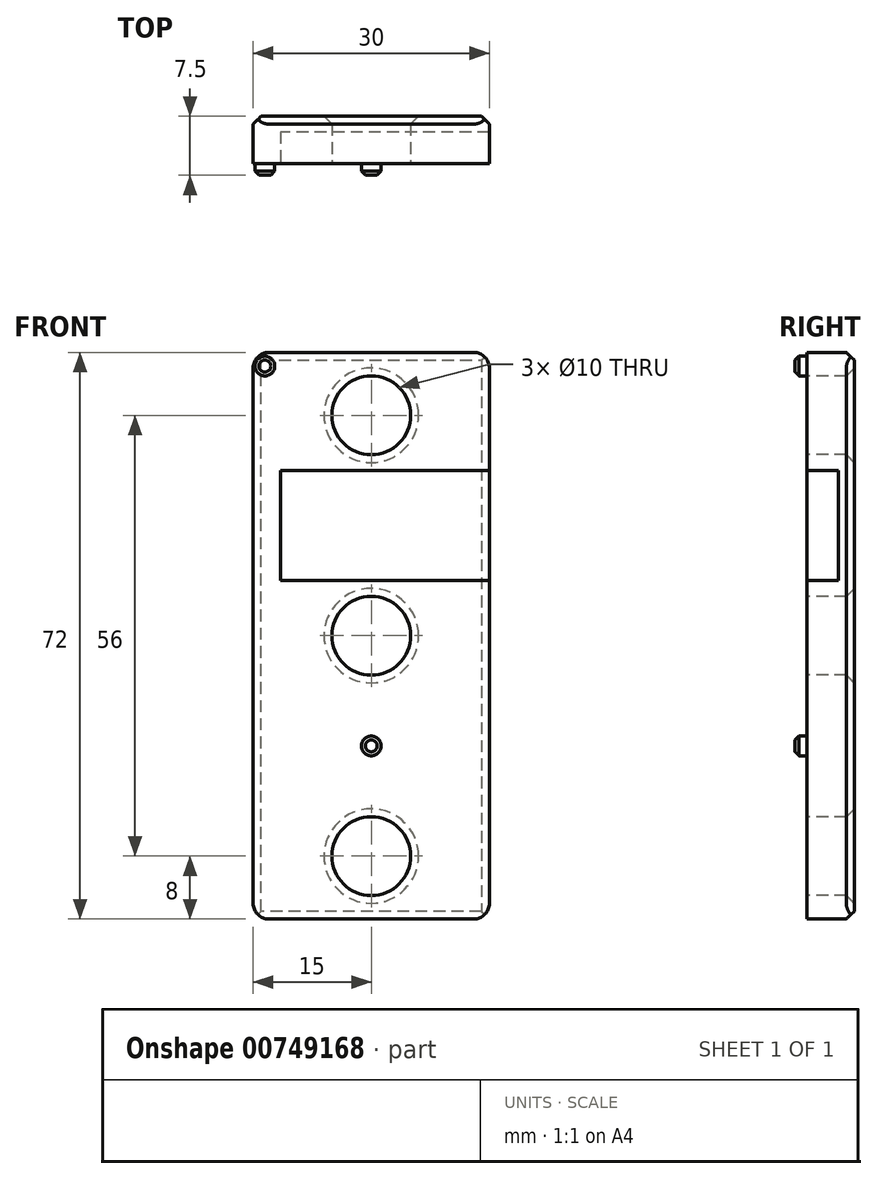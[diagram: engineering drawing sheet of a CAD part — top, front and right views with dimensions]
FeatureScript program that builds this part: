
annotation { "Feature Type Name" : "Feature", "Feature Type Description" : "" }
export const myFeature = defineFeature(function(context is Context, id is Id, definition is map)
    precondition{}
    {
        {
            var Q0;
            Q0=qCreatedBy(makeId("Front.planeOp"),FACE);
            var sketch = newSketch(context, id + "F0", { "sketchPlane" : qUnion([Q0])});
            skLineSegment(sketch, "E0.bottom", {"start": v(-15, 8) * mm, "end": v(15, 8) * mm});
            skLineSegment(sketch, "E0.top", {"start": v(-15, -64) * mm, "end": v(15, -64) * mm});
            skLineSegment(sketch, "E0.left", {"start": v(-15, 8) * mm, "end": v(-15, -64) * mm});
            skLineSegment(sketch, "E0.right", {"start": v(15, 8) * mm, "end": v(15, -64) * mm});
            skCircle(sketch, "E1", {"center": v(0, 0) * mm, "radius": 5 * mm});
            skCircle(sketch, "E2", {"center": v(0, -28) * mm, "radius": 5 * mm});
            skCircle(sketch, "E3", {"center": v(0, -56) * mm, "radius": 5 * mm});
            skSolve(sketch);
        }
        {
            var Q0;
            Q0 = qSketchRegion(id + "F0", true);
            extrude(context, id + "F1", {"entities" : qUnion([Q0]), "oppositeDirection" : true, "depth" : 6 * mm, "offsetDistance" : 25 * mm});
        }
        {
            var Q0;
            Q0=qCreatedBy(makeId("Front.planeOp"),FACE);
            var sketch = newSketch(context, id + "F2", { "sketchPlane" : qUnion([Q0])});
            skCircle(sketch, "E4", {"center": v(-13.5, 6.25) * mm, "radius": 1.25 * mm});
            skCircle(sketch, "E5", {"center": v(0, -42) * mm, "radius": 1.25 * mm});
            skSolve(sketch);
        }
        {
            var Q0;
            Q0 = qSketchRegion(id + "F2", true);
            extrude(context, id + "F3", {"entities" : qUnion([Q0]), "operationType" : NewBodyOperationType.ADD, "depth" : 1.5 * mm, "offsetDistance" : 25 * mm});
        }
        {
            var Q0;
            Q0=makeQuery(id+"F3.opExtrude","CAP_EDGE",EDGE,{"disambiguationData":[OSD([sQuery(id+"F2.wireOp",EDGE,"E4")])],"isStart":false});
            var Q1;
            Q1=makeQuery(id+"F3.opExtrude","CAP_EDGE",EDGE,{"disambiguationData":[OSD([sQuery(id+"F2.wireOp",EDGE,"E5")])],"isStart":false});
            chamfer(context, id + "F4", {"entities" : qUnion([Q0, Q1]), "width" : 0.5 * mm, "tangentPropagation" : true});
        }
        {
            var Q0;
            Q0=makeQuery(id+"F1.opExtrude","CAP_EDGE",EDGE,{"disambiguationData":[OSD([sQuery(id+"F0.wireOp",EDGE,"E3")])],"isStart":false});
            var Q1;
            Q1=makeQuery(id+"F1.opExtrude","CAP_EDGE",EDGE,{"disambiguationData":[OSD([sQuery(id+"F0.wireOp",EDGE,"E2")])],"isStart":false});
            var Q2;
            Q2=makeQuery(id+"F1.opExtrude","CAP_EDGE",EDGE,{"disambiguationData":[OSD([sQuery(id+"F0.wireOp",EDGE,"E1")])],"isStart":false});
            var Q3;
            Q3=makeQuery(id+"F1.opExtrude","CAP_EDGE",EDGE,{"disambiguationData":[OSD([sQuery(id+"F0.wireOp",EDGE,"E0.left")])],"isStart":false});
            var Q4;
            Q4=makeQuery(id+"F1.opExtrude","CAP_EDGE",EDGE,{"disambiguationData":[OSD([sQuery(id+"F0.wireOp",EDGE,"E0.top")])],"isStart":false});
            var Q5;
            Q5=makeQuery(id+"F1.opExtrude","CAP_EDGE",EDGE,{"disambiguationData":[OSD([sQuery(id+"F0.wireOp",EDGE,"E0.bottom")])],"isStart":false});
            var Q6;
            Q6=makeQuery(id+"F1.opExtrude","CAP_EDGE",EDGE,{"disambiguationData":[OSD([sQuery(id+"F0.wireOp",EDGE,"E0.right")])],"isStart":false});
            chamfer(context, id + "F5", {"entities" : qUnion([Q0, Q1, Q2, Q3, Q4, Q5, Q6]), "width" : 1 * mm, "tangentPropagation" : true});
        }
        {
            var Q0;
            Q0=makeQuery(id+"F1.opExtrude","SWEPT_EDGE",EDGE,{"disambiguationData":[OSD([sQuery(id+"F0.wireOp",EDGE,"E0.bottom"),sQuery(id+"F0.wireOp",EDGE,"E0.left")])]});
            var Q1;
            Q1=makeQuery(id+"F1.opExtrude","SWEPT_EDGE",EDGE,{"disambiguationData":[OSD([sQuery(id+"F0.wireOp",EDGE,"E0.bottom"),sQuery(id+"F0.wireOp",EDGE,"E0.right")])]});
            var Q2;
            Q2=makeQuery(id+"F1.opExtrude","SWEPT_EDGE",EDGE,{"disambiguationData":[OSD([sQuery(id+"F0.wireOp",EDGE,"E0.top"),sQuery(id+"F0.wireOp",EDGE,"E0.right")])]});
            var Q3;
            Q3=makeQuery(id+"F1.opExtrude","SWEPT_EDGE",EDGE,{"disambiguationData":[OSD([sQuery(id+"F0.wireOp",EDGE,"E0.top"),sQuery(id+"F0.wireOp",EDGE,"E0.left")])]});
            fillet(context, id + "F6", {"entities" : qUnion([Q0, Q1, Q2, Q3]), "radius" : 2 * mm, "tangentPropagation" : true, "allowEdgeOverflow" : false});
        }
        {
            var Q0;
            Q0=qCreatedBy(makeId("Front.planeOp"),FACE);
            var sketch = newSketch(context, id + "F7", { "sketchPlane" : qUnion([Q0])});
            skLineSegment(sketch, "E6.bottom", {"start": v(22.81, -7) * mm, "end": v(-11.5, -7) * mm});
            skLineSegment(sketch, "E6.top", {"start": v(22.81, -21) * mm, "end": v(-11.5, -21) * mm});
            skLineSegment(sketch, "E6.left", {"start": v(22.81, -7) * mm, "end": v(22.81, -21) * mm});
            skLineSegment(sketch, "E6.right", {"start": v(-11.5, -7) * mm, "end": v(-11.5, -21) * mm});
            skSolve(sketch);
        }
        {
            var Q0;
            Q0 = qSketchRegion(id + "F7", true);
            extrude(context, id + "F8", {"entities" : qUnion([Q0]), "operationType" : NewBodyOperationType.REMOVE, "oppositeDirection" : true, "depth" : 4 * mm, "offsetDistance" : 25 * mm});
        }
    });
